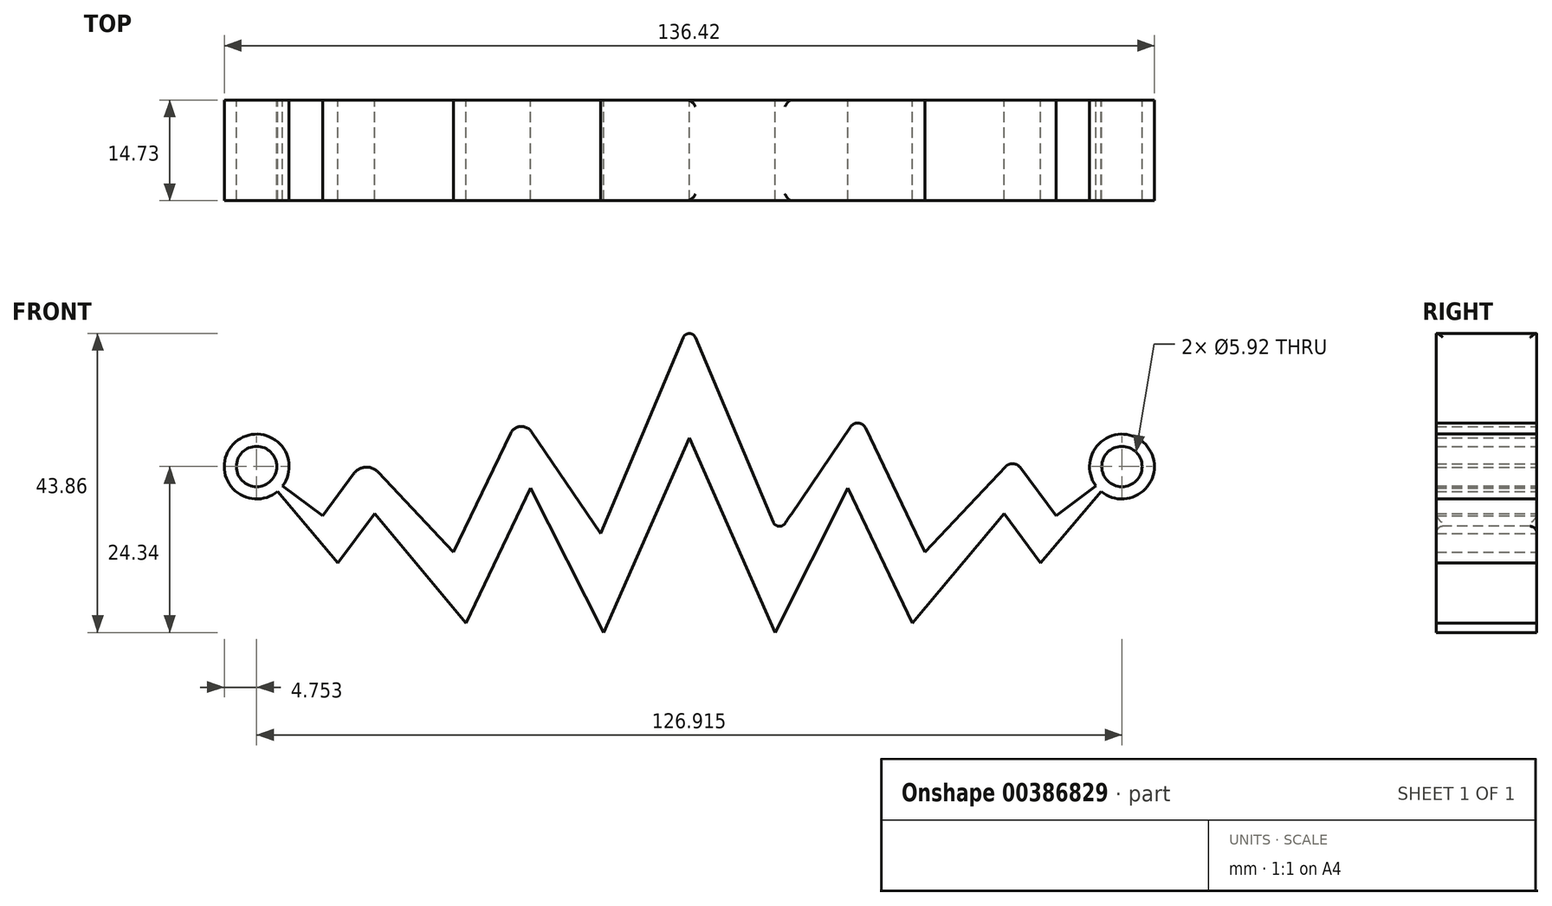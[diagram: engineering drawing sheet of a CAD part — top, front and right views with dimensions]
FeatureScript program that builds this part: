
annotation { "Feature Type Name" : "Feature", "Feature Type Description" : "" }
export const myFeature = defineFeature(function(context is Context, id is Id, definition is map)
    precondition{}
    {
        {
            var Q0;
            Q0=qCreatedBy(makeId("Front.planeOp"),FACE);
            var sketch = newSketch(context, id + "F0", { "sketchPlane" : qUnion([Q0])});
            skLineSegment(sketch, "E0", {"start": v(0, 24.2) * mm, "end": v(13.03, -6.66) * mm});
            skLineSegment(sketch, "E1", {"start": v(13.03, -6.66) * mm, "end": v(24.89, 10.8) * mm});
            skLineSegment(sketch, "E2", {"start": v(24.89, 10.8) * mm, "end": v(34.56, -9.41) * mm});
            skLineSegment(sketch, "E3", {"start": v(34.56, -9.41) * mm, "end": v(47.54, 4.33) * mm});
            skLineSegment(sketch, "E4", {"start": v(47.54, 4.33) * mm, "end": v(53.8, -4.06) * mm});
            skLineSegment(sketch, "E5", {"start": v(53.8, -4.06) * mm, "end": v(59.65, 0.3) * mm});
            skLineSegment(sketch, "E6", {"start": v(60.39, -0.48) * mm, "end": v(51.54, -10.97) * mm});
            skLineSegment(sketch, "E7", {"start": v(51.54, -10.97) * mm, "end": v(46.17, -3.76) * mm});
            skLineSegment(sketch, "E8", {"start": v(46.17, -3.76) * mm, "end": v(32.74, -19.81) * mm});
            skLineSegment(sketch, "E9", {"start": v(32.74, -19.81) * mm, "end": v(23.26, 0) * mm});
            skLineSegment(sketch, "E10", {"start": v(23.26, 0) * mm, "end": v(12.58, -21.2) * mm});
            skLineSegment(sketch, "E11", {"start": v(12.58, -21.2) * mm, "end": v(0, 7.39) * mm});
            skArc(sketch, "E12", {"start": v(60.39, -0.48) * mm, "mid": v(66.92, 6.4) * mm, "end": v(59.65, 0.3) * mm});
            skLineSegment(sketch, "E13.MirrorCS", {"start": v(0, 24.2) * mm, "end": v(-13.03, -6.66) * mm});
            skLineSegment(sketch, "E14.MirrorCS", {"start": v(-12.58, -21.2) * mm, "end": v(0, 7.39) * mm});
            skLineSegment(sketch, "E15.MirrorCS", {"start": v(-13.03, -6.66) * mm, "end": v(-24.89, 10.8) * mm});
            skLineSegment(sketch, "E16.MirrorCS", {"start": v(-23.26, 0) * mm, "end": v(-12.58, -21.2) * mm});
            skLineSegment(sketch, "E17.MirrorCS", {"start": v(-24.89, 10.8) * mm, "end": v(-34.56, -9.41) * mm});
            skLineSegment(sketch, "E18.MirrorCS", {"start": v(-32.74, -19.81) * mm, "end": v(-23.26, 0) * mm});
            skLineSegment(sketch, "E19.MirrorCS", {"start": v(-34.56, -9.41) * mm, "end": v(-47.54, 4.33) * mm});
            skLineSegment(sketch, "E20.MirrorCS", {"start": v(-46.17, -3.76) * mm, "end": v(-32.74, -19.81) * mm});
            skLineSegment(sketch, "E21.MirrorCS", {"start": v(-47.54, 4.33) * mm, "end": v(-53.8, -4.06) * mm});
            skLineSegment(sketch, "E22.MirrorCS", {"start": v(-51.54, -10.97) * mm, "end": v(-46.17, -3.76) * mm});
            skLineSegment(sketch, "E23.MirrorCS", {"start": v(-53.8, -4.06) * mm, "end": v(-59.65, 0.3) * mm});
            skLineSegment(sketch, "E24.MirrorCS", {"start": v(-60.39, -0.48) * mm, "end": v(-51.54, -10.97) * mm});
            skCircle(sketch, "E25", {"center": v(63.46, 3.15) * mm, "radius": 2.96 * mm});
            skPoint(sketch, "E26.orphan", {"position": v(-63.46, 3.15) * mm});
            skCircle(sketch, "E27.MirrorC", {"center": v(-63.46, 3.15) * mm, "radius": 2.96 * mm});
            skArc(sketch, "E28.MirrorCS", {"start": v(-60.39, -0.48) * mm, "mid": v(-66.92, 6.4) * mm, "end": v(-59.65, 0.3) * mm});
            skSolve(sketch);
        }
        {
            var Q0;
            Q0=makeQuery(id+"F0.imprint","IMPRINT",FACE,{"disambiguationData":[TD([[makeQuery(id+"F0.imprint","IMPRINT",EDGE,{"derivedFrom":sQuery(id+"F0.wireOp",EDGE,"E0")}),-1.0]])]});
            extrude(context, id + "F1", {"entities" : qUnion([Q0]), "depth" : 14.73 * mm});
        }
        {
            var Q0;
            Q0=makeQuery(id+"F1.opExtrude","SWEPT_FACE",FACE,{"disambiguationData":[OSD([sQuery(id+"F0.wireOp",EDGE,"E0")])]});
            var Q1;
            Q1=makeQuery(id+"F1.opExtrude","SWEPT_EDGE",EDGE,{"disambiguationData":[OSD([sQuery(id+"F0.wireOp",EDGE,"E0"),sQuery(id+"F0.wireOp",EDGE,"E13.MirrorCS")])]});
            fillet(context, id + "F2", {"entities" : qUnion([Q0, Q1]), "radius" : 0.97 * mm, "tangentPropagation" : true, "allowEdgeOverflow" : false});
        }
        {
            var Q0;
            Q0=makeQuery(id+"F1.opExtrude","SWEPT_EDGE",EDGE,{"disambiguationData":[OSD([sQuery(id+"F0.wireOp",EDGE,"E15.MirrorCS"),sQuery(id+"F0.wireOp",EDGE,"E17.MirrorCS")])]});
            fillet(context, id + "F3", {"entities" : qUnion([Q0]), "radius" : 1.77 * mm, "tangentPropagation" : true, "allowEdgeOverflow" : false});
        }
        {
            var Q0;
            Q0=makeQuery(id+"F1.opExtrude","SWEPT_EDGE",EDGE,{"disambiguationData":[OSD([sQuery(id+"F0.wireOp",EDGE,"E1"),sQuery(id+"F0.wireOp",EDGE,"E2")])]});
            fillet(context, id + "F4", {"entities" : qUnion([Q0]), "radius" : 1.26 * mm, "tangentPropagation" : true, "allowEdgeOverflow" : false});
        }
        {
            var Q0;
            Q0=makeQuery(id+"F1.opExtrude","SWEPT_EDGE",EDGE,{"disambiguationData":[OSD([sQuery(id+"F0.wireOp",EDGE,"E19.MirrorCS"),sQuery(id+"F0.wireOp",EDGE,"E21.MirrorCS")])]});
            fillet(context, id + "F5", {"entities" : qUnion([Q0]), "radius" : 2.3 * mm, "tangentPropagation" : true, "allowEdgeOverflow" : false});
        }
        {
            var Q0;
            Q0=makeQuery(id+"F1.opExtrude","SWEPT_EDGE",EDGE,{"disambiguationData":[OSD([sQuery(id+"F0.wireOp",EDGE,"E3"),sQuery(id+"F0.wireOp",EDGE,"E4")])]});
            fillet(context, id + "F6", {"entities" : qUnion([Q0]), "radius" : 1.37 * mm, "tangentPropagation" : true, "allowEdgeOverflow" : false});
        }
    });
